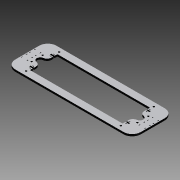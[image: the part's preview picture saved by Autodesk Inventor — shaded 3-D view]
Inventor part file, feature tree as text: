
AUTODESK INVENTOR PART (.ipt)
format: ipt  version: 2013 (Build 170138000, 138)  size: 305,664 bytes
history: native  units: mm
features: extrude x4, sketch x4, mirror x3, fillet x1
ambient origin geometry x8: Origin, YZ Plane, XZ Plane, XY Plane, X Axis, Y Axis, Z Axis, Center Point
bodies: Solid1 (feature_tree)
feature tree (12):
  extrude  "Extrusion1"  Depth=70.0mm
  fillet  "Fillet1"  Radius=30.0mm
  extrude  "Extrusion2"  Depth=4.0mm
  mirror  "Mirror1"
  mirror  "Mirror2"
  extrude  "Extrusion3"  Depth=10.0mm
  mirror  "Mirror3"
  extrude  "Extrusion4"  Depth=16.0mm
  sketch  "Sketch1"  dims[d0=130.0mm d1=70.0mm d2=30.0mm]
  sketch  "Sketch2"  dims[d3=20.0mm d4=4.0mm]
  sketch  "Sketch3"  dims[d5=10.0mm d6=10.0mm]
  sketch  "Sketch5"  dims[d7=145.0mm d8=16.0mm d9=16.0mm d10=16.0mm d11=7.5mm d13=24.0mm d14=11.5mm d15=183.0mm d16=5.715mm d17=0.0mm d18=5.0mm d19=2.0mm d20=25.0mm d21=8.0mm d23=1.5mm d24=4.0mm d25=5.0mm d26=7.5mm d27=6.477mm d28=0.0mm d29=15.0mm d31=10.0mm d32=7.5mm d34=20.0mm d35=10.0mm d36=10.0mm d37=0.0mm d38=18.0mm d42=10.0mm d43=0.0mm]
